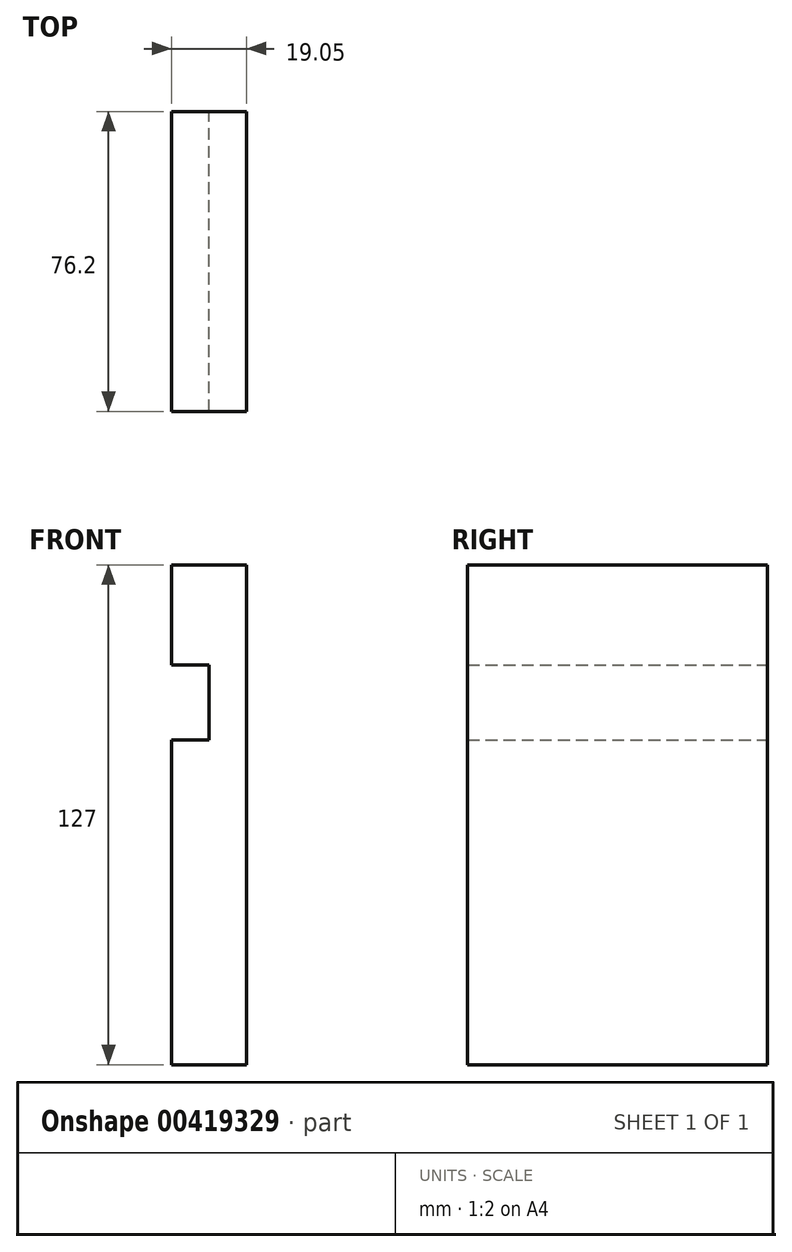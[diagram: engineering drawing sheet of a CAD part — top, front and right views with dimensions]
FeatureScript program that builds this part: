
annotation { "Feature Type Name" : "Feature", "Feature Type Description" : "" }
export const myFeature = defineFeature(function(context is Context, id is Id, definition is map)
    precondition{}
    {
        {
            var Q0;
            Q0=qCreatedBy(makeId("Front.planeOp"),FACE);
            var sketch = newSketch(context, id + "F0", { "sketchPlane" : qUnion([Q0])});
            skLineSegment(sketch, "E0", {"start": v(0, 0) * mm, "end": v(-19.05, 0) * mm});
            skLineSegment(sketch, "E1", {"start": v(0, 0) * mm, "end": v(0, 127) * mm});
            skLineSegment(sketch, "E2", {"start": v(0, 127) * mm, "end": v(-19.05, 127) * mm});
            skLineSegment(sketch, "E3", {"start": v(-19.05, 127) * mm, "end": v(-19.05, 101.6) * mm});
            skLineSegment(sketch, "E4", {"start": v(-19.05, 101.6) * mm, "end": v(-9.52, 101.6) * mm});
            skLineSegment(sketch, "E5", {"start": v(-9.52, 101.6) * mm, "end": v(-9.52, 82.55) * mm});
            skLineSegment(sketch, "E6", {"start": v(-9.52, 82.55) * mm, "end": v(-19.05, 82.55) * mm});
            skLineSegment(sketch, "E7", {"start": v(-19.05, 82.55) * mm, "end": v(-19.05, 0) * mm});
            skSolve(sketch);
        }
        {
            var Q0;
            Q0=makeQuery(id+"F0.imprint","IMPRINT",FACE,{"disambiguationData":[TD([[makeQuery(id+"F0.imprint","IMPRINT",EDGE,{"derivedFrom":sQuery(id+"F0.wireOp",EDGE,"E0")}),-1.0]])]});
            extrude(context, id + "F1", {"entities" : qUnion([Q0]), "depth" : 76.2 * mm});
        }
    });
